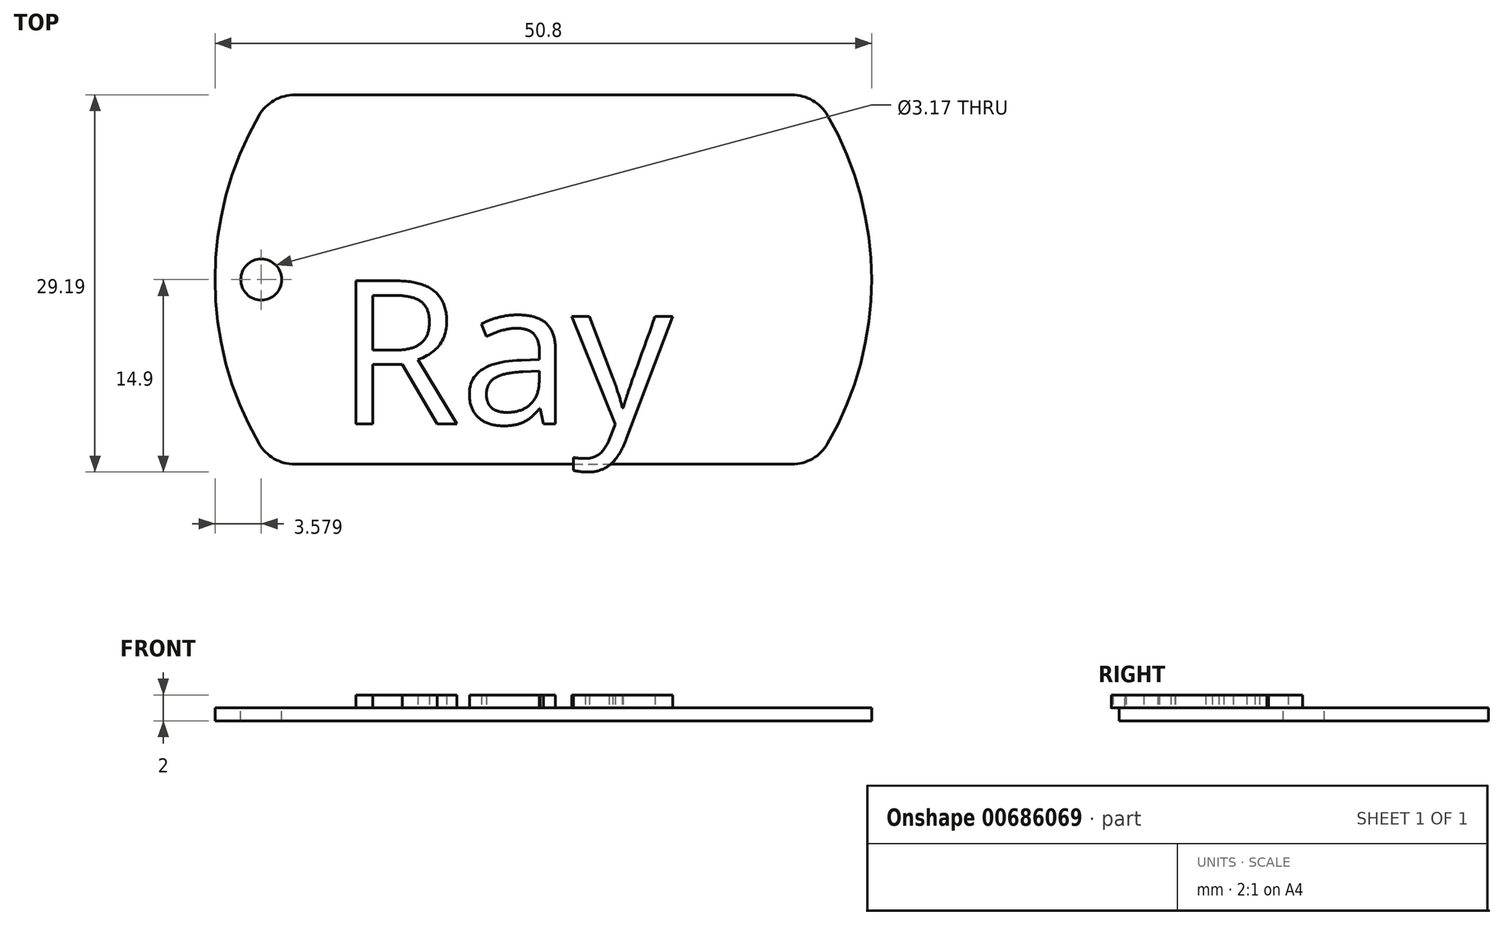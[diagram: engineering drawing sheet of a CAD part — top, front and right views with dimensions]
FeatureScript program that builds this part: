
annotation { "Feature Type Name" : "Feature", "Feature Type Description" : "" }
export const myFeature = defineFeature(function(context is Context, id is Id, definition is map)
    precondition{}
    {
        {
            var Q0;
            Q0=qCreatedBy(makeId("Top.planeOp"),FACE);
            var sketch = newSketch(context, id + "F0", { "sketchPlane" : qUnion([Q0])});
            skArc(sketch, "E0", {"start": v(-22, 12.7) * mm, "mid": v(-25.4, 0) * mm, "end": v(-22, -12.7) * mm});
            skLineSegment(sketch, "E1.top", {"start": v(-19.25, -14.29) * mm, "end": v(19.25, -14.29) * mm});
            skArc(sketch, "E2.trimOffspring", {"start": v(22, -12.7) * mm, "mid": v(25.4, 0) * mm, "end": v(22, 12.7) * mm});
            skLineSegment(sketch, "E3", {"start": v(-19.25, 14.29) * mm, "end": v(19.25, 14.29) * mm});
            skPoint(sketch, "E4.visualSharp", {"position": v(-21, 14.29) * mm});
            skArc(sketch, "E4.filletArc", {"start": v(-19.25, 14.29) * mm, "mid": v(-20.83, 13.86) * mm, "end": v(-22, 12.7) * mm});
            skPoint(sketch, "E5.visualSharp", {"position": v(21, 14.29) * mm});
            skArc(sketch, "E5.filletArc", {"start": v(22, 12.7) * mm, "mid": v(20.83, 13.86) * mm, "end": v(19.25, 14.29) * mm});
            skPoint(sketch, "E6.visualSharp", {"position": v(21, -14.29) * mm});
            skArc(sketch, "E6.filletArc", {"start": v(19.25, -14.29) * mm, "mid": v(20.83, -13.86) * mm, "end": v(22, -12.7) * mm});
            skPoint(sketch, "E7.visualSharp", {"position": v(-21, -14.29) * mm});
            skArc(sketch, "E7.filletArc", {"start": v(-22, -12.7) * mm, "mid": v(-20.83, -13.86) * mm, "end": v(-19.25, -14.29) * mm});
            skSolve(sketch);
        }
        {
            var Q0;
            Q0=makeQuery(id+"F0.imprint","IMPRINT",FACE,{"disambiguationData":[TD([[makeQuery(id+"F0.imprint","IMPRINT",EDGE,{"derivedFrom":sQuery(id+"F0.wireOp",EDGE,"E0")}),1.0]])]});
            extrude(context, id + "F1", {"entities" : qUnion([Q0]), "depth" : 1 * mm, "offsetDistance" : 25.4 * mm});
        }
        {
            var Q0;
            Q0=makeQuery(id+"F1.opExtrude","CAP_FACE",FACE,{"disambiguationData":[OSD([sQuery(id+"F0.wireOp",EDGE,"E0"),sQuery(id+"F0.wireOp",EDGE,"E1.top"),sQuery(id+"F0.wireOp",EDGE,"E2.trimOffspring"),sQuery(id+"F0.wireOp",EDGE,"E3"),sQuery(id+"F0.wireOp",EDGE,"E4.filletArc"),sQuery(id+"F0.wireOp",EDGE,"E5.filletArc"),sQuery(id+"F0.wireOp",EDGE,"E6.filletArc"),sQuery(id+"F0.wireOp",EDGE,"E7.filletArc")])],"isStart":false});
            var sketch = newSketch(context, id + "F2", { "sketchPlane" : qUnion([Q0])});
            skLineSegment(sketch, "E8.0", {"start": v(-18.66, 13.29) * mm, "end": v(18.66, 13.29) * mm});
            skArc(sketch, "E8.1", {"start": v(-21.45, 11.63) * mm, "mid": v(-24.4, 0) * mm, "end": v(-21.45, -11.63) * mm});
            skLineSegment(sketch, "E8.2", {"start": v(-18.66, -13.29) * mm, "end": v(18.66, -13.29) * mm});
            skArc(sketch, "E8.3", {"start": v(21.45, -11.63) * mm, "mid": v(24.4, 0) * mm, "end": v(21.45, 11.63) * mm});
            skPoint(sketch, "E9.visualSharp", {"position": v(-20.46, 13.29) * mm});
            skArc(sketch, "E9.filletArc", {"start": v(-18.66, 13.29) * mm, "mid": v(-20.29, 12.84) * mm, "end": v(-21.45, 11.63) * mm});
            skPoint(sketch, "E10.visualSharp", {"position": v(20.46, 13.29) * mm});
            skArc(sketch, "E10.filletArc", {"start": v(21.45, 11.63) * mm, "mid": v(20.29, 12.84) * mm, "end": v(18.66, 13.29) * mm});
            skPoint(sketch, "E11.visualSharp", {"position": v(20.46, -13.29) * mm});
            skArc(sketch, "E11.filletArc", {"start": v(18.66, -13.29) * mm, "mid": v(20.29, -12.84) * mm, "end": v(21.45, -11.63) * mm});
            skPoint(sketch, "E12.visualSharp", {"position": v(-20.46, -13.29) * mm});
            skArc(sketch, "E12.filletArc", {"start": v(-21.45, -11.63) * mm, "mid": v(-20.29, -12.84) * mm, "end": v(-18.66, -13.29) * mm});
            skLineSegment(sketch, "E13.0", {"start": v(-19.25, 14.29) * mm, "end": v(19.25, 14.29) * mm});
            skArc(sketch, "E13.1", {"start": v(-22, 12.7) * mm, "mid": v(-25.4, 0) * mm, "end": v(-22, -12.7) * mm});
            skLineSegment(sketch, "E13.2", {"start": v(-19.25, -14.29) * mm, "end": v(19.25, -14.29) * mm});
            skArc(sketch, "E13.3", {"start": v(22, -12.7) * mm, "mid": v(25.4, 0) * mm, "end": v(22, 12.7) * mm});
            skPoint(sketch, "E14.visualSharp", {"position": v(-21, -14.29) * mm});
            skArc(sketch, "E14.filletArc", {"start": v(-22, -12.7) * mm, "mid": v(-20.83, -13.86) * mm, "end": v(-19.25, -14.29) * mm});
            skPoint(sketch, "E15.visualSharp", {"position": v(21, -14.29) * mm});
            skArc(sketch, "E15.filletArc", {"start": v(19.25, -14.29) * mm, "mid": v(20.83, -13.86) * mm, "end": v(22, -12.7) * mm});
            skPoint(sketch, "E16.visualSharp", {"position": v(21, 14.29) * mm});
            skArc(sketch, "E16.filletArc", {"start": v(22, 12.7) * mm, "mid": v(20.83, 13.86) * mm, "end": v(19.25, 14.29) * mm});
            skPoint(sketch, "E17.visualSharp", {"position": v(-21, 14.29) * mm});
            skArc(sketch, "E17.filletArc", {"start": v(-19.25, 14.29) * mm, "mid": v(-20.83, 13.86) * mm, "end": v(-22, 12.7) * mm});
            skSolve(sketch);
        }
        {
            var Q0;
            Q0=makeQuery(id+"F1.opExtrude","CAP_FACE",FACE,{"disambiguationData":[OSD([sQuery(id+"F0.wireOp",EDGE,"E0"),sQuery(id+"F0.wireOp",EDGE,"E1.top"),sQuery(id+"F0.wireOp",EDGE,"E2.trimOffspring"),sQuery(id+"F0.wireOp",EDGE,"E3"),sQuery(id+"F0.wireOp",EDGE,"E4.filletArc"),sQuery(id+"F0.wireOp",EDGE,"E5.filletArc"),sQuery(id+"F0.wireOp",EDGE,"E6.filletArc"),sQuery(id+"F0.wireOp",EDGE,"E7.filletArc")])],"isStart":false});
            var sketch = newSketch(context, id + "F3", { "sketchPlane" : qUnion([Q0])});
            skCircle(sketch, "E18", {"center": v(-21.82, 0) * mm, "radius": 1.59 * mm});
            skSolve(sketch);
        }
        {
            var Q0;
            Q0=makeQuery(id+"F3.imprint","IMPRINT",FACE,{"disambiguationData":[TD([[makeQuery(id+"F3.imprint","IMPRINT",EDGE,{"derivedFrom":sQuery(id+"F3.wireOp",EDGE,"E18")}),1.0]])]});
            extrude(context, id + "F4", {"entities" : qUnion([Q0]), "operationType" : NewBodyOperationType.REMOVE, "oppositeDirection" : true, "depth" : 1 * mm, "offsetDistance" : 25.4 * mm});
        }
        {
            var Q0;
            Q0=makeQuery(id+"F2.imprint","IMPRINT",FACE,{"disambiguationData":[TD([[makeQuery(id+"F2.imprint","IMPRINT",EDGE,{"derivedFrom":sQuery(id+"F2.wireOp",EDGE,"E8.0")}),-1.0]])]});
            var sketch = newSketch(context, id + "F5", { "sketchPlane" : qUnion([Q0])});
            skText(sketch, "E19", { "text": "Ray", "fontName": "OpenSans-Regular.ttf"});
            const initialGuessF5  = {"E19": [-0.01602, -0.01117, 1, 0, 0.01117]};
            skSetInitialGuess(sketch, initialGuessF5);
            skSolve(sketch);
        }
        {
            var Q0;
            Q0 = qSketchRegion(id + "F5", true);
            extrude(context, id + "F6", {"entities" : qUnion([Q0]), "operationType" : NewBodyOperationType.ADD, "depth" : 1 * mm, "offsetDistance" : 25.4 * mm});
        }
    });
